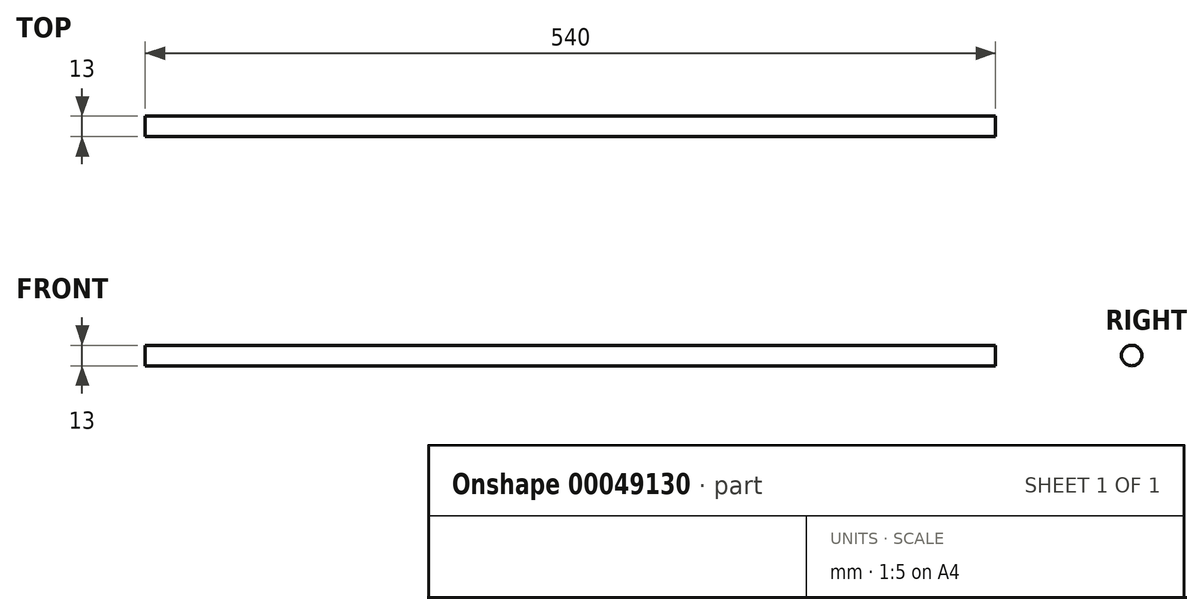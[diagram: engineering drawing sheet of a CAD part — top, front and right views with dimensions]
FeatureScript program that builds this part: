
annotation { "Feature Type Name" : "Feature", "Feature Type Description" : "" }
export const myFeature = defineFeature(function(context is Context, id is Id, definition is map)
    precondition{}
    {
        {
            var Q0;
            Q0=qCreatedBy(makeId("Top.planeOp"),FACE);
            var sketch = newSketch(context, id + "F0", { "sketchPlane" : qUnion([Q0])});
            skLineSegment(sketch, "E0.bottom", {"start": v(-75.32, 0) * mm, "end": v(464.68, 0) * mm});
            skLineSegment(sketch, "E0.top", {"start": v(-75.32, 6.5) * mm, "end": v(464.68, 6.5) * mm});
            skLineSegment(sketch, "E0.left", {"start": v(-75.32, 0) * mm, "end": v(-75.32, 6.5) * mm});
            skLineSegment(sketch, "E0.right", {"start": v(464.68, 0) * mm, "end": v(464.68, 6.5) * mm});
            skSolve(sketch);
        }
        {
            var Q0;
            Q0 = qSketchRegion(id + "F0", true);
            var Q1;
            Q1=sQuery(id+"F0.wireOp",EDGE,"E0.bottom");
            revolve(context, id + "F1", {"entities" : qUnion([Q0]), "axis" : qUnion([Q1]), "revolveType" : RevolveType.FULL});
        }
    });
